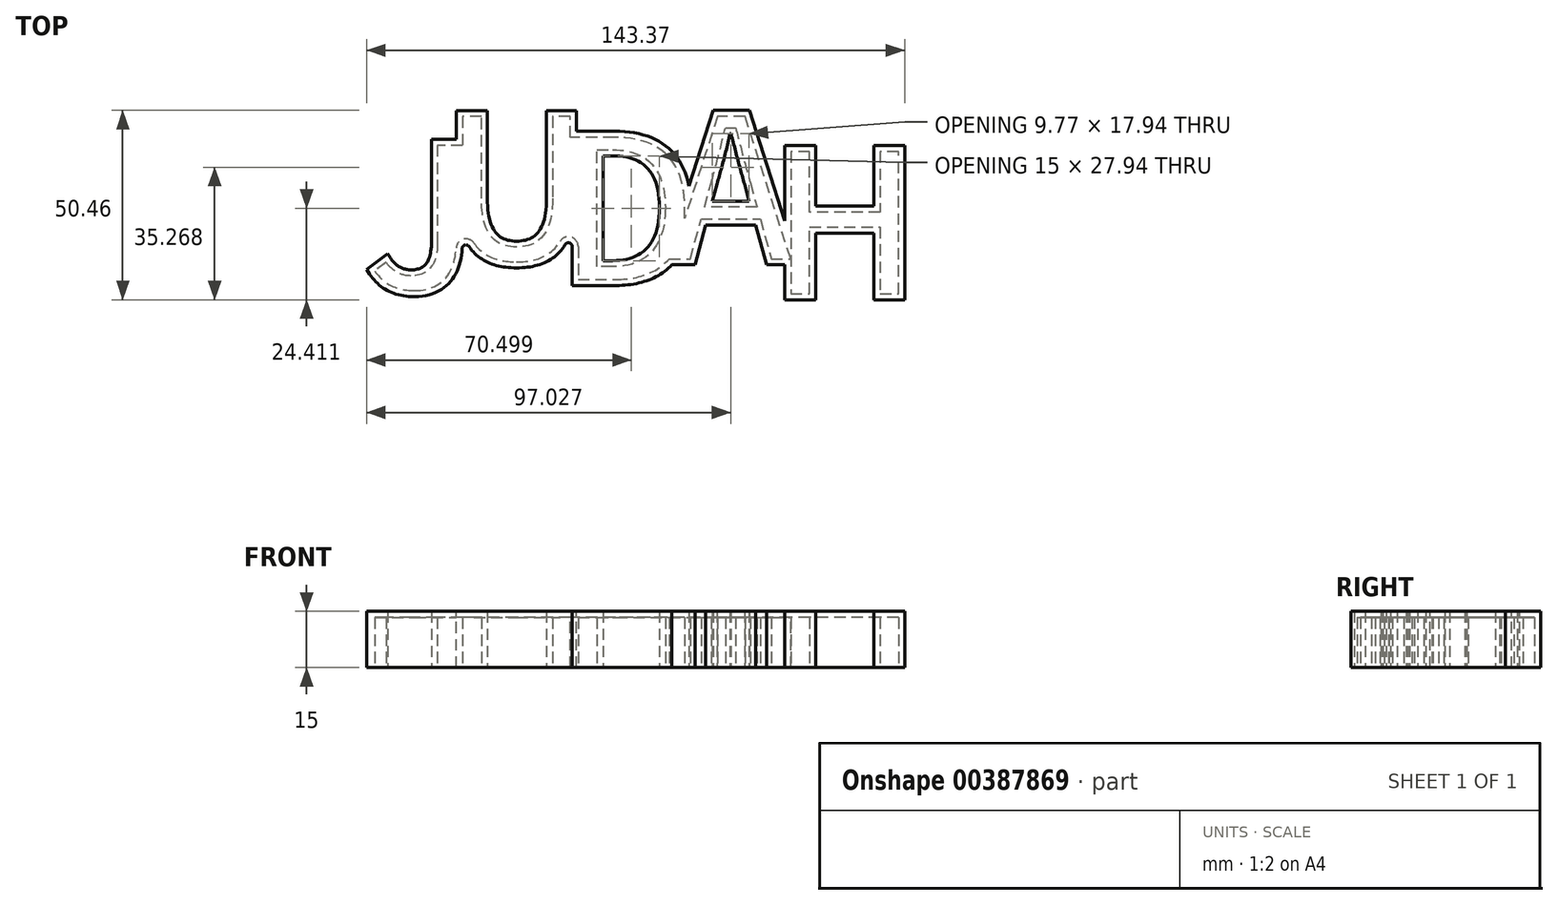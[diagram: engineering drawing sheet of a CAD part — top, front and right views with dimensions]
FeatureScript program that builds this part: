
annotation { "Feature Type Name" : "Feature", "Feature Type Description" : "" }
export const myFeature = defineFeature(function(context is Context, id is Id, definition is map)
    precondition{}
    {
        {
            var Q0;
            Q0=qCreatedBy(makeId("Top.planeOp"),FACE);
            var sketch = newSketch(context, id + "F0", { "sketchPlane" : qUnion([Q0])});
            skText(sketch, "E0", { "text": "J U D A H", "fontName": "NotoSansCJKsc-Bold.otf"});
            const initialGuessF0  = {"E0": [-0.10786, 0.03175, 1, 0, 0.04]};
            skSetInitialGuess(sketch, initialGuessF0);
            skSolve(sketch);
        }
        {
            var Q0;
            Q0 = qSketchRegion(id + "F0", true);
            extrude(context, id + "F1", {"entities" : qUnion([Q0]), "depth" : 15 * mm});
        }
        {
            var Q0;
            Q0=qCreatedBy(makeId("Top.planeOp"),FACE);
            var sketch = newSketch(context, id + "F2", { "sketchPlane" : qUnion([Q0])});
            skPoint(sketch, "E1.0", {"position": v(-58.86, 72.86) * mm});
            skLineSegment(sketch, "E2", {"start": v(-58.86, 72.86) * mm, "end": v(-82.68, 80.51) * mm});
            skSolve(sketch);
        }
        {
            var Q0;
            Q0=makeQuery(id+"F1.opExtrude","SWEPT_BODY",BODY,{"disambiguationData":[OSD([sQuery(id+"F0.wireOp",EDGE,"E0.sketch_text.stroke-8"),sQuery(id+"F0.wireOp",EDGE,"E0.sketch_text.stroke-9"),sQuery(id+"F0.wireOp",EDGE,"E0.sketch_text.stroke-10"),sQuery(id+"F0.wireOp",EDGE,"E0.sketch_text.stroke-11"),sQuery(id+"F0.wireOp",EDGE,"E0.sketch_text.stroke-12"),sQuery(id+"F0.wireOp",EDGE,"E0.sketch_text.stroke-13"),sQuery(id+"F0.wireOp",EDGE,"E0.sketch_text.stroke-14"),sQuery(id+"F0.wireOp",EDGE,"E0.sketch_text.stroke-15"),sQuery(id+"F0.wireOp",EDGE,"E0.sketch_text.stroke-16"),sQuery(id+"F0.wireOp",EDGE,"E0.sketch_text.stroke-17")])]});
            var Q1;
            Q1=sQuery(id+"F2.wireOp",EDGE,"E2");
            transform(context, id + "F3", {"entities" : qUnion([Q0]), "transformType" : TransformType.TRANSLATION_ENTITY, "oppositeDirectionEntity" : false, "transformLine" : qUnion([Q1]), "makeCopy" : false});
        }
        {
            var Q0;
            Q0=qCreatedBy(makeId("Top.planeOp"),FACE);
            var sketch = newSketch(context, id + "F4", { "sketchPlane" : qUnion([Q0])});
            skPoint(sketch, "E3.0", {"position": v(-4.47, 31.75) * mm});
            skLineSegment(sketch, "E4", {"start": v(-4.47, 31.75) * mm, "end": v(-51.87, 33.93) * mm});
            skSolve(sketch);
        }
        {
            var Q0;
            Q0=makeQuery(id+"F1.opExtrude","SWEPT_BODY",BODY,{"disambiguationData":[OSD([sQuery(id+"F0.wireOp",EDGE,"E0.sketch_text.stroke-18"),sQuery(id+"F0.wireOp",EDGE,"E0.sketch_text.stroke-19"),sQuery(id+"F0.wireOp",EDGE,"E0.sketch_text.stroke-20"),sQuery(id+"F0.wireOp",EDGE,"E0.sketch_text.stroke-21"),sQuery(id+"F0.wireOp",EDGE,"E0.sketch_text.stroke-22"),sQuery(id+"F0.wireOp",EDGE,"E0.sketch_text.stroke-23"),sQuery(id+"F0.wireOp",EDGE,"E0.sketch_text.stroke-24"),sQuery(id+"F0.wireOp",EDGE,"E0.sketch_text.stroke-25"),sQuery(id+"F0.wireOp",EDGE,"E0.sketch_text.stroke-26"),sQuery(id+"F0.wireOp",EDGE,"E0.sketch_text.stroke-27")])]});
            var Q1;
            Q1=sQuery(id+"F4.wireOp",EDGE,"E4");
            transform(context, id + "F5", {"entities" : qUnion([Q0]), "transformType" : TransformType.TRANSLATION_ENTITY, "oppositeDirectionEntity" : false, "transformLine" : qUnion([Q1]), "makeCopy" : false});
        }
        {
            var Q0;
            Q0=qCreatedBy(makeId("Top.planeOp"),FACE);
            var sketch = newSketch(context, id + "F6", { "sketchPlane" : qUnion([Q0])});
            skPoint(sketch, "E5.0", {"position": v(42.53, 31.75) * mm});
            skLineSegment(sketch, "E6", {"start": v(42.53, 31.75) * mm, "end": v(-27.5, 39.46) * mm});
            skSolve(sketch);
        }
        {
            var Q0;
            Q0=makeQuery(id+"F1.opExtrude","SWEPT_BODY",BODY,{"disambiguationData":[OSD([sQuery(id+"F0.wireOp",EDGE,"E0.sketch_text.stroke-28"),sQuery(id+"F0.wireOp",EDGE,"E0.sketch_text.stroke-29"),sQuery(id+"F0.wireOp",EDGE,"E0.sketch_text.stroke-30"),sQuery(id+"F0.wireOp",EDGE,"E0.sketch_text.stroke-31"),sQuery(id+"F0.wireOp",EDGE,"E0.sketch_text.stroke-32"),sQuery(id+"F0.wireOp",EDGE,"E0.sketch_text.stroke-33"),sQuery(id+"F0.wireOp",EDGE,"E0.sketch_text.stroke-34"),sQuery(id+"F0.wireOp",EDGE,"E0.sketch_text.stroke-35"),sQuery(id+"F0.wireOp",EDGE,"E0.sketch_text.stroke-36"),sQuery(id+"F0.wireOp",EDGE,"E0.sketch_text.stroke-37"),sQuery(id+"F0.wireOp",EDGE,"E0.sketch_text.stroke-38"),sQuery(id+"F0.wireOp",EDGE,"E0.sketch_text.stroke-39"),sQuery(id+"F0.wireOp",EDGE,"E0.sketch_text.stroke-40"),sQuery(id+"F0.wireOp",EDGE,"E0.sketch_text.stroke-41")])]});
            var Q1;
            Q1=sQuery(id+"F6.wireOp",EDGE,"E6");
            transform(context, id + "F7", {"entities" : qUnion([Q0]), "transformType" : TransformType.TRANSLATION_ENTITY, "oppositeDirectionEntity" : false, "transformLine" : qUnion([Q1]), "makeCopy" : false});
        }
        {
            var Q0;
            Q0=qCreatedBy(makeId("Top.planeOp"),FACE);
            var sketch = newSketch(context, id + "F8", { "sketchPlane" : qUnion([Q0])});
            skPoint(sketch, "E7.0", {"position": v(96.03, 31.75) * mm});
            skLineSegment(sketch, "E8", {"start": v(96.03, 31.75) * mm, "end": v(4.79, 30.11) * mm});
            skSolve(sketch);
        }
        {
            var Q0;
            Q0=makeQuery(id+"F1.opExtrude","SWEPT_BODY",BODY,{"disambiguationData":[OSD([sQuery(id+"F0.wireOp",EDGE,"E0.sketch_text.stroke-42"),sQuery(id+"F0.wireOp",EDGE,"E0.sketch_text.stroke-43"),sQuery(id+"F0.wireOp",EDGE,"E0.sketch_text.stroke-44"),sQuery(id+"F0.wireOp",EDGE,"E0.sketch_text.stroke-45"),sQuery(id+"F0.wireOp",EDGE,"E0.sketch_text.stroke-46"),sQuery(id+"F0.wireOp",EDGE,"E0.sketch_text.stroke-47"),sQuery(id+"F0.wireOp",EDGE,"E0.sketch_text.stroke-48"),sQuery(id+"F0.wireOp",EDGE,"E0.sketch_text.stroke-49"),sQuery(id+"F0.wireOp",EDGE,"E0.sketch_text.stroke-50"),sQuery(id+"F0.wireOp",EDGE,"E0.sketch_text.stroke-51"),sQuery(id+"F0.wireOp",EDGE,"E0.sketch_text.stroke-52"),sQuery(id+"F0.wireOp",EDGE,"E0.sketch_text.stroke-53")])]});
            var Q1;
            Q1=sQuery(id+"F8.wireOp",EDGE,"E8");
            transform(context, id + "F9", {"entities" : qUnion([Q0]), "transformType" : TransformType.TRANSLATION_ENTITY, "oppositeDirectionEntity" : false, "transformLine" : qUnion([Q1]), "makeCopy" : false});
        }
        {
            var Q0;
            Q0=makeQuery(id+"F1.opExtrude","SWEPT_BODY",BODY,{"disambiguationData":[OSD([sQuery(id+"F0.wireOp",EDGE,"E0.sketch_text.stroke-0"),sQuery(id+"F0.wireOp",EDGE,"E0.sketch_text.stroke-1"),sQuery(id+"F0.wireOp",EDGE,"E0.sketch_text.stroke-2"),sQuery(id+"F0.wireOp",EDGE,"E0.sketch_text.stroke-3"),sQuery(id+"F0.wireOp",EDGE,"E0.sketch_text.stroke-4"),sQuery(id+"F0.wireOp",EDGE,"E0.sketch_text.stroke-5"),sQuery(id+"F0.wireOp",EDGE,"E0.sketch_text.stroke-6"),sQuery(id+"F0.wireOp",EDGE,"E0.sketch_text.stroke-7")])]});
            var Q1;
            Q1=makeQuery(id+"F1.opExtrude","SWEPT_BODY",BODY,{"disambiguationData":[OSD([sQuery(id+"F0.wireOp",EDGE,"E0.sketch_text.stroke-8"),sQuery(id+"F0.wireOp",EDGE,"E0.sketch_text.stroke-9"),sQuery(id+"F0.wireOp",EDGE,"E0.sketch_text.stroke-10"),sQuery(id+"F0.wireOp",EDGE,"E0.sketch_text.stroke-11"),sQuery(id+"F0.wireOp",EDGE,"E0.sketch_text.stroke-12"),sQuery(id+"F0.wireOp",EDGE,"E0.sketch_text.stroke-13"),sQuery(id+"F0.wireOp",EDGE,"E0.sketch_text.stroke-14"),sQuery(id+"F0.wireOp",EDGE,"E0.sketch_text.stroke-15"),sQuery(id+"F0.wireOp",EDGE,"E0.sketch_text.stroke-16"),sQuery(id+"F0.wireOp",EDGE,"E0.sketch_text.stroke-17")])]});
            var Q2;
            Q2=makeQuery(id+"F1.opExtrude","SWEPT_BODY",BODY,{"disambiguationData":[OSD([sQuery(id+"F0.wireOp",EDGE,"E0.sketch_text.stroke-18"),sQuery(id+"F0.wireOp",EDGE,"E0.sketch_text.stroke-19"),sQuery(id+"F0.wireOp",EDGE,"E0.sketch_text.stroke-20"),sQuery(id+"F0.wireOp",EDGE,"E0.sketch_text.stroke-21"),sQuery(id+"F0.wireOp",EDGE,"E0.sketch_text.stroke-22"),sQuery(id+"F0.wireOp",EDGE,"E0.sketch_text.stroke-23"),sQuery(id+"F0.wireOp",EDGE,"E0.sketch_text.stroke-24"),sQuery(id+"F0.wireOp",EDGE,"E0.sketch_text.stroke-25"),sQuery(id+"F0.wireOp",EDGE,"E0.sketch_text.stroke-26"),sQuery(id+"F0.wireOp",EDGE,"E0.sketch_text.stroke-27")])]});
            var Q3;
            Q3=makeQuery(id+"F1.opExtrude","SWEPT_BODY",BODY,{"disambiguationData":[OSD([sQuery(id+"F0.wireOp",EDGE,"E0.sketch_text.stroke-28"),sQuery(id+"F0.wireOp",EDGE,"E0.sketch_text.stroke-29"),sQuery(id+"F0.wireOp",EDGE,"E0.sketch_text.stroke-30"),sQuery(id+"F0.wireOp",EDGE,"E0.sketch_text.stroke-31"),sQuery(id+"F0.wireOp",EDGE,"E0.sketch_text.stroke-32"),sQuery(id+"F0.wireOp",EDGE,"E0.sketch_text.stroke-33"),sQuery(id+"F0.wireOp",EDGE,"E0.sketch_text.stroke-34"),sQuery(id+"F0.wireOp",EDGE,"E0.sketch_text.stroke-35"),sQuery(id+"F0.wireOp",EDGE,"E0.sketch_text.stroke-36"),sQuery(id+"F0.wireOp",EDGE,"E0.sketch_text.stroke-37"),sQuery(id+"F0.wireOp",EDGE,"E0.sketch_text.stroke-38"),sQuery(id+"F0.wireOp",EDGE,"E0.sketch_text.stroke-39"),sQuery(id+"F0.wireOp",EDGE,"E0.sketch_text.stroke-40"),sQuery(id+"F0.wireOp",EDGE,"E0.sketch_text.stroke-41")])]});
            var Q4;
            Q4=makeQuery(id+"F1.opExtrude","SWEPT_BODY",BODY,{"disambiguationData":[OSD([sQuery(id+"F0.wireOp",EDGE,"E0.sketch_text.stroke-42"),sQuery(id+"F0.wireOp",EDGE,"E0.sketch_text.stroke-43"),sQuery(id+"F0.wireOp",EDGE,"E0.sketch_text.stroke-44"),sQuery(id+"F0.wireOp",EDGE,"E0.sketch_text.stroke-45"),sQuery(id+"F0.wireOp",EDGE,"E0.sketch_text.stroke-46"),sQuery(id+"F0.wireOp",EDGE,"E0.sketch_text.stroke-47"),sQuery(id+"F0.wireOp",EDGE,"E0.sketch_text.stroke-48"),sQuery(id+"F0.wireOp",EDGE,"E0.sketch_text.stroke-49"),sQuery(id+"F0.wireOp",EDGE,"E0.sketch_text.stroke-50"),sQuery(id+"F0.wireOp",EDGE,"E0.sketch_text.stroke-51"),sQuery(id+"F0.wireOp",EDGE,"E0.sketch_text.stroke-52"),sQuery(id+"F0.wireOp",EDGE,"E0.sketch_text.stroke-53")])]});
            booleanBodies(context, id + "F10", {"operationType" : BooleanOperationType.UNION, "tools" : qUnion([Q0, Q1, Q2, Q3, Q4])});
        }
        {
            var Q0;
            Q0=makeQuery(id+"F10.opBoolean","INTERSECT",EDGE,{"derivedFrom":[makeQuery(id+"F1.opExtrude","SWEPT_FACE",FACE,{"disambiguationData":[OSD([sQuery(id+"F0.wireOp",EDGE,"E0.sketch_text.stroke-1")])]}),makeQuery(id+"F1.opExtrude","SWEPT_FACE",FACE,{"disambiguationData":[OSD([sQuery(id+"F0.wireOp",EDGE,"E0.sketch_text.stroke-17")])]})]});
            var Q1;
            Q1=makeQuery(id+"F10.opBoolean","INTERSECT",EDGE,{"derivedFrom":[makeQuery(id+"F1.opExtrude","SWEPT_FACE",FACE,{"disambiguationData":[OSD([sQuery(id+"F0.wireOp",EDGE,"E0.sketch_text.stroke-8")])]}),makeQuery(id+"F1.opExtrude","SWEPT_FACE",FACE,{"disambiguationData":[OSD([sQuery(id+"F0.wireOp",EDGE,"E0.sketch_text.stroke-22")])]})]});
            fillet(context, id + "F11", {"entities" : qUnion([Q0, Q1]), "radius" : 1 * mm, "tangentPropagation" : true, "allowEdgeOverflow" : false});
        }
        {
            var Q0;
            Q0=makeQuery(id+"F10.opBoolean","MERGE",FACE,{"derivedFrom":[makeQuery(id+"F1.opExtrude","CAP_FACE",FACE,{"disambiguationData":[OSD([sQuery(id+"F0.wireOp",EDGE,"E0.sketch_text.stroke-0"),sQuery(id+"F0.wireOp",EDGE,"E0.sketch_text.stroke-1"),sQuery(id+"F0.wireOp",EDGE,"E0.sketch_text.stroke-2"),sQuery(id+"F0.wireOp",EDGE,"E0.sketch_text.stroke-3"),sQuery(id+"F0.wireOp",EDGE,"E0.sketch_text.stroke-4"),sQuery(id+"F0.wireOp",EDGE,"E0.sketch_text.stroke-5"),sQuery(id+"F0.wireOp",EDGE,"E0.sketch_text.stroke-6"),sQuery(id+"F0.wireOp",EDGE,"E0.sketch_text.stroke-7")])],"isStart":true}),makeQuery(id+"F1.opExtrude","CAP_FACE",FACE,{"disambiguationData":[OSD([sQuery(id+"F0.wireOp",EDGE,"E0.sketch_text.stroke-8"),sQuery(id+"F0.wireOp",EDGE,"E0.sketch_text.stroke-9"),sQuery(id+"F0.wireOp",EDGE,"E0.sketch_text.stroke-10"),sQuery(id+"F0.wireOp",EDGE,"E0.sketch_text.stroke-11"),sQuery(id+"F0.wireOp",EDGE,"E0.sketch_text.stroke-12"),sQuery(id+"F0.wireOp",EDGE,"E0.sketch_text.stroke-13"),sQuery(id+"F0.wireOp",EDGE,"E0.sketch_text.stroke-14"),sQuery(id+"F0.wireOp",EDGE,"E0.sketch_text.stroke-15"),sQuery(id+"F0.wireOp",EDGE,"E0.sketch_text.stroke-16"),sQuery(id+"F0.wireOp",EDGE,"E0.sketch_text.stroke-17")])],"isStart":true}),makeQuery(id+"F1.opExtrude","CAP_FACE",FACE,{"disambiguationData":[OSD([sQuery(id+"F0.wireOp",EDGE,"E0.sketch_text.stroke-18"),sQuery(id+"F0.wireOp",EDGE,"E0.sketch_text.stroke-19"),sQuery(id+"F0.wireOp",EDGE,"E0.sketch_text.stroke-20"),sQuery(id+"F0.wireOp",EDGE,"E0.sketch_text.stroke-21"),sQuery(id+"F0.wireOp",EDGE,"E0.sketch_text.stroke-22"),sQuery(id+"F0.wireOp",EDGE,"E0.sketch_text.stroke-23"),sQuery(id+"F0.wireOp",EDGE,"E0.sketch_text.stroke-24"),sQuery(id+"F0.wireOp",EDGE,"E0.sketch_text.stroke-25"),sQuery(id+"F0.wireOp",EDGE,"E0.sketch_text.stroke-26"),sQuery(id+"F0.wireOp",EDGE,"E0.sketch_text.stroke-27")])],"isStart":true}),makeQuery(id+"F1.opExtrude","CAP_FACE",FACE,{"disambiguationData":[OSD([sQuery(id+"F0.wireOp",EDGE,"E0.sketch_text.stroke-28"),sQuery(id+"F0.wireOp",EDGE,"E0.sketch_text.stroke-29"),sQuery(id+"F0.wireOp",EDGE,"E0.sketch_text.stroke-30"),sQuery(id+"F0.wireOp",EDGE,"E0.sketch_text.stroke-31"),sQuery(id+"F0.wireOp",EDGE,"E0.sketch_text.stroke-32"),sQuery(id+"F0.wireOp",EDGE,"E0.sketch_text.stroke-33"),sQuery(id+"F0.wireOp",EDGE,"E0.sketch_text.stroke-34"),sQuery(id+"F0.wireOp",EDGE,"E0.sketch_text.stroke-35"),sQuery(id+"F0.wireOp",EDGE,"E0.sketch_text.stroke-36"),sQuery(id+"F0.wireOp",EDGE,"E0.sketch_text.stroke-37"),sQuery(id+"F0.wireOp",EDGE,"E0.sketch_text.stroke-38"),sQuery(id+"F0.wireOp",EDGE,"E0.sketch_text.stroke-39"),sQuery(id+"F0.wireOp",EDGE,"E0.sketch_text.stroke-40"),sQuery(id+"F0.wireOp",EDGE,"E0.sketch_text.stroke-41")])],"isStart":true}),makeQuery(id+"F1.opExtrude","CAP_FACE",FACE,{"disambiguationData":[OSD([sQuery(id+"F0.wireOp",EDGE,"E0.sketch_text.stroke-42"),sQuery(id+"F0.wireOp",EDGE,"E0.sketch_text.stroke-43"),sQuery(id+"F0.wireOp",EDGE,"E0.sketch_text.stroke-44"),sQuery(id+"F0.wireOp",EDGE,"E0.sketch_text.stroke-45"),sQuery(id+"F0.wireOp",EDGE,"E0.sketch_text.stroke-46"),sQuery(id+"F0.wireOp",EDGE,"E0.sketch_text.stroke-47"),sQuery(id+"F0.wireOp",EDGE,"E0.sketch_text.stroke-48"),sQuery(id+"F0.wireOp",EDGE,"E0.sketch_text.stroke-49"),sQuery(id+"F0.wireOp",EDGE,"E0.sketch_text.stroke-50"),sQuery(id+"F0.wireOp",EDGE,"E0.sketch_text.stroke-51"),sQuery(id+"F0.wireOp",EDGE,"E0.sketch_text.stroke-52"),sQuery(id+"F0.wireOp",EDGE,"E0.sketch_text.stroke-53")])],"isStart":true})]});
            shell(context, id + "F12", {"entities" : qUnion([Q0]), "thickness" : 1.6 * mm});
        }
    });
